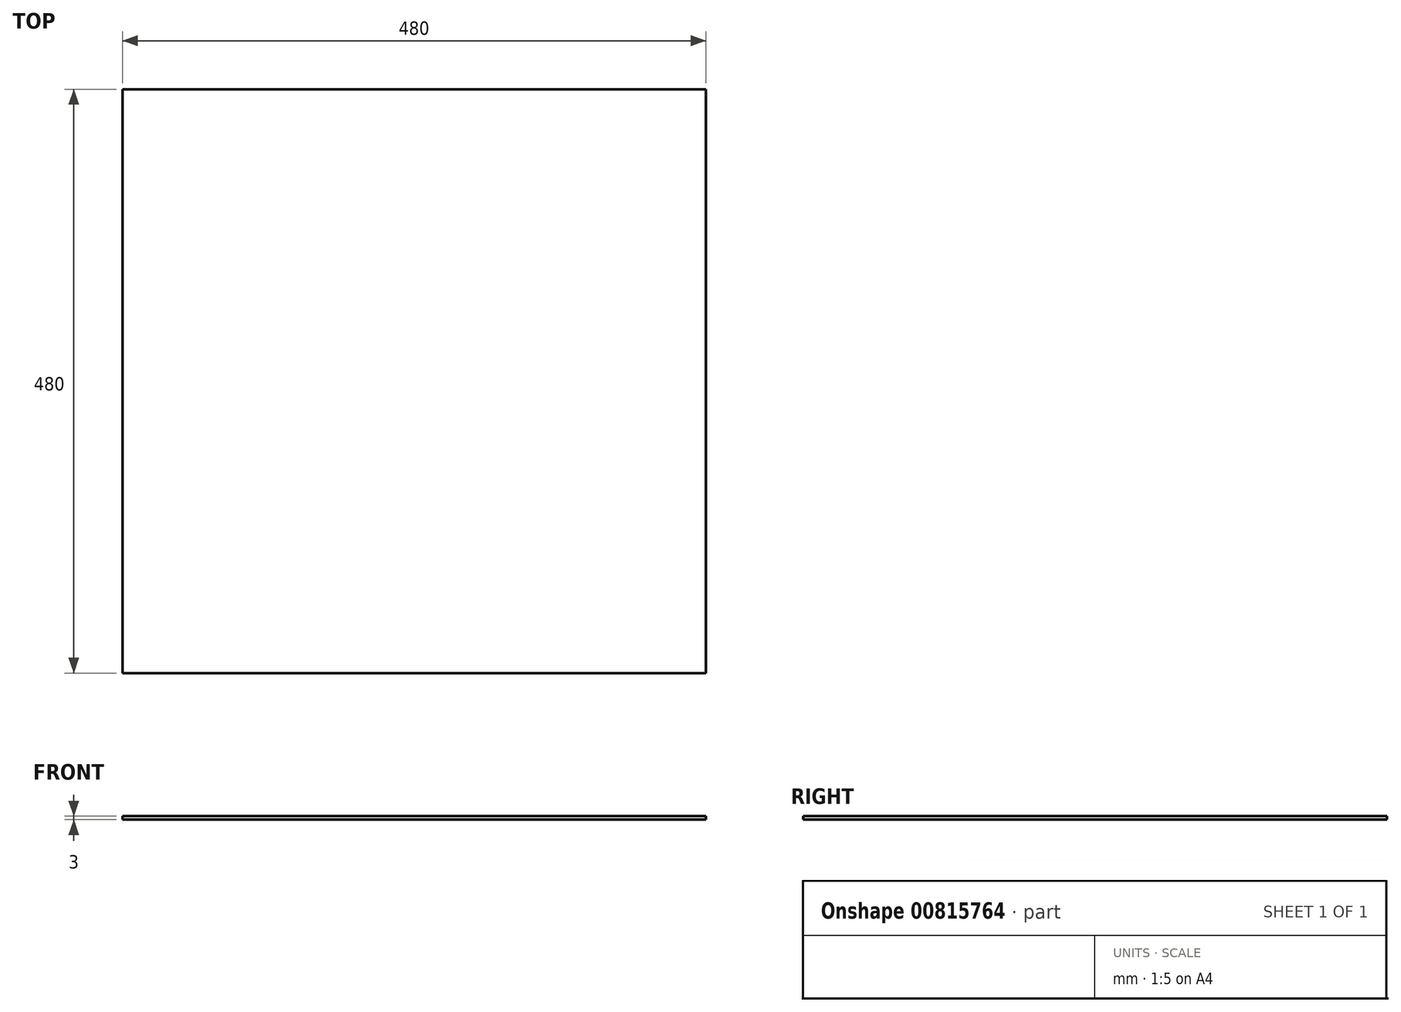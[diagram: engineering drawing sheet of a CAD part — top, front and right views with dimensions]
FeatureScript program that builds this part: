
annotation { "Feature Type Name" : "Feature", "Feature Type Description" : "" }
export const myFeature = defineFeature(function(context is Context, id is Id, definition is map)
    precondition{}
    {
        {
            var Q0;
            Q0=qCreatedBy(makeId("Top.planeOp"),FACE);
            var sketch = newSketch(context, id + "F0", { "sketchPlane" : qUnion([Q0])});
            skLineSegment(sketch, "E0.bottom", {"start": v(240, -240) * mm, "end": v(-240, -240) * mm});
            skLineSegment(sketch, "E0.top", {"start": v(240, 240) * mm, "end": v(-240, 240) * mm});
            skLineSegment(sketch, "E0.left", {"start": v(240, -240) * mm, "end": v(240, 240) * mm});
            skLineSegment(sketch, "E0.right", {"start": v(-240, -240) * mm, "end": v(-240, 240) * mm});
            skPoint(sketch, "E0.middle", {"position": v(0, 0) * mm});
            skSolve(sketch);
        }
        {
            var Q0;
            Q0=makeQuery(id+"F0.imprint","IMPRINT",FACE,{"disambiguationData":[TD([[makeQuery(id+"F0.imprint","IMPRINT",EDGE,{"derivedFrom":sQuery(id+"F0.wireOp",EDGE,"E0.bottom")}),-1.0]])]});
            extrude(context, id + "F1", {"entities" : qUnion([Q0]), "depth" : 3 * mm, "offsetDistance" : 25 * mm});
        }
    });
